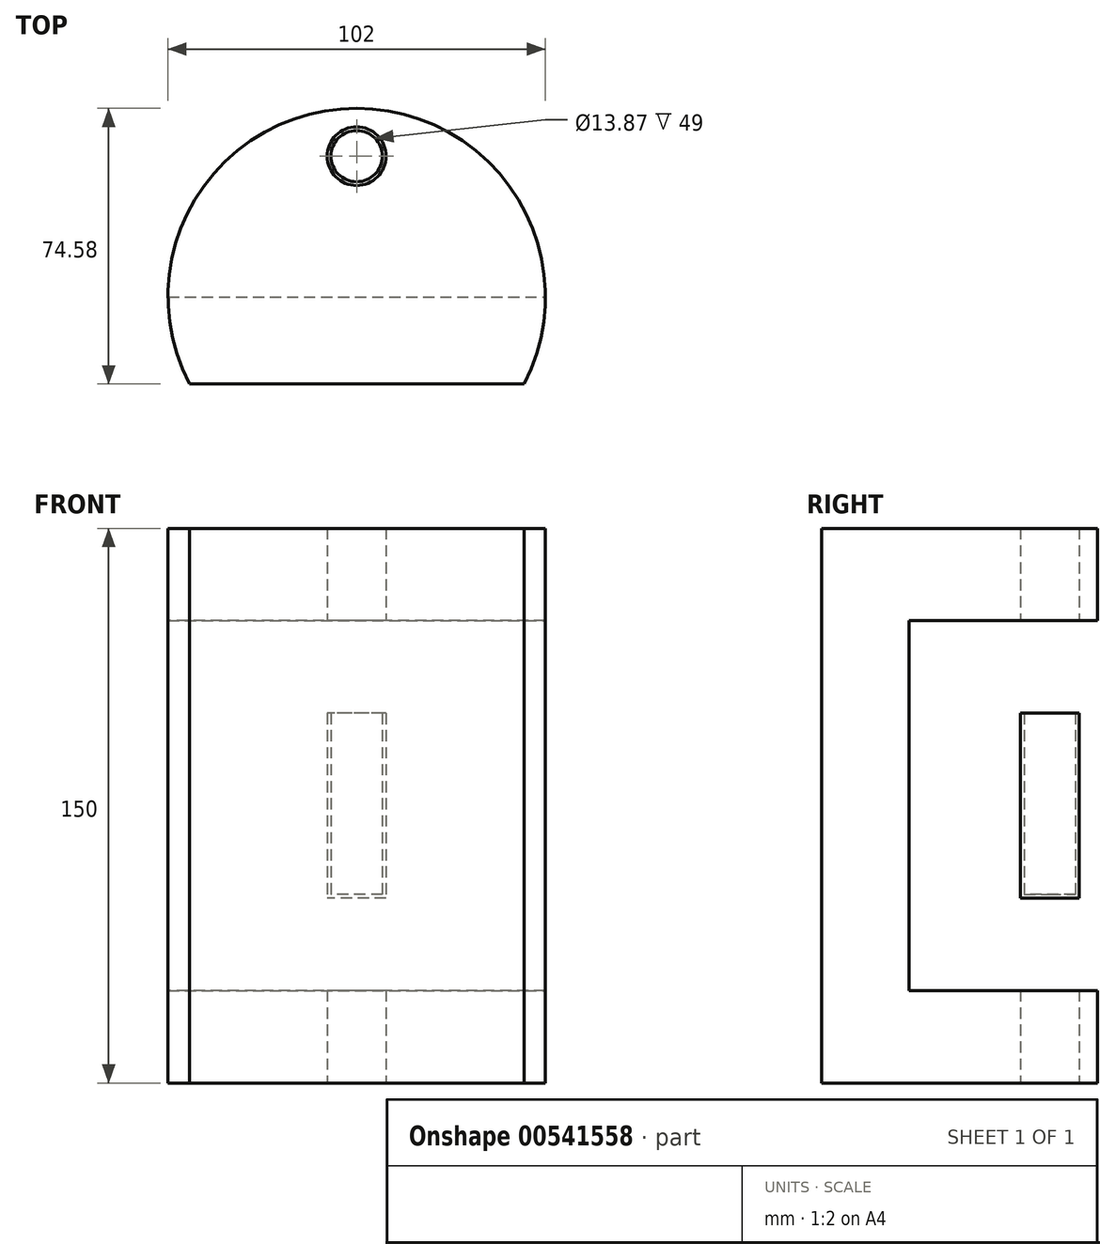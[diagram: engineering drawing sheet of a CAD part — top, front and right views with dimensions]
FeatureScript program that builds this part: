
annotation { "Feature Type Name" : "Feature", "Feature Type Description" : "" }
export const myFeature = defineFeature(function(context is Context, id is Id, definition is map)
    precondition{}
    {
        {
            var Q0;
            Q0=qCreatedBy(makeId("Top.planeOp"),FACE);
            var sketch = newSketch(context, id + "F0", { "sketchPlane" : qUnion([Q0])});
            skArc(sketch, "E0", {"start": v(45.22, -23.58) * mm, "mid": v(0, 51) * mm, "end": v(-45.22, -23.58) * mm});
            skLineSegment(sketch, "E1", {"start": v(0, -23.58) * mm, "end": v(45.22, -23.58) * mm});
            skLineSegment(sketch, "E2", {"start": v(0, -23.58) * mm, "end": v(-45.22, -23.58) * mm});
            skLineSegment(sketch, "E3", {"start": v(-51, 0) * mm, "end": v(51, 0) * mm});
            skCircle(sketch, "E4", {"center": v(0, 38.05) * mm, "radius": 7.94 * mm});
            skSolve(sketch);
        }
        {
            var Q0;
            {var subQ0=sQuery(id+"F0.wireOp",EDGE,"E3");Q0=makeQuery(id+"F0.imprint","IMPRINT",FACE,{"disambiguationData":[TD([[makeQuery(id+"F0.imprint","IMPRINT",EDGE,{"derivedFrom":subQ0}),1.0]])]});}
            extrude(context, id + "F1", {"entities" : qUnion([Q0]), "depth" : 75 * mm, "offsetDistance" : 25 * mm, "hasSecondDirection" : true, "secondDirectionOppositeDirection" : true, "secondDirectionDepth" : 75 * mm});
        }
        {
            var Q0;
            {var subQ1=sQuery(id+"F0.wireOp",EDGE,"E1");Q0=makeQuery(id+"F0.imprint","IMPRINT",FACE,{"disambiguationData":[TD([[makeQuery(id+"F0.imprint","IMPRINT",EDGE,{"derivedFrom":subQ1}),1.0]])]});}
            extrude(context, id + "F2", {"entities" : qUnion([Q0]), "operationType" : NewBodyOperationType.ADD, "depth" : 75 * mm, "offsetDistance" : 25 * mm, "hasSecondDirection" : true, "secondDirectionOppositeDirection" : true, "secondDirectionDepth" : 75 * mm});
        }
        {
            var Q0;
            {var subQ0=sQuery(id+"F0.wireOp",EDGE,"E3");Q0=makeQuery(id+"F0.imprint","IMPRINT",FACE,{"disambiguationData":[TD([[makeQuery(id+"F0.imprint","IMPRINT",EDGE,{"derivedFrom":subQ0}),1.0]])]});}
            extrude(context, id + "F3", {"entities" : qUnion([Q0]), "operationType" : NewBodyOperationType.REMOVE, "oppositeDirection" : true, "depth" : 50 * mm, "offsetDistance" : 25 * mm, "hasSecondDirection" : true, "secondDirectionOppositeDirection" : false, "secondDirectionDepth" : 50 * mm});
        }
        {
            var Q0;
            Q0=makeQuery(id+"F0.imprint","IMPRINT",FACE,{"disambiguationData":[TD([[makeQuery(id+"F0.imprint","IMPRINT",EDGE,{"derivedFrom":sQuery(id+"F0.wireOp",EDGE,"E4")}),1.0]])]});
            var Q1;
            Q1=sQuery(id+"F0.wireOp",EDGE,"E4");
            extrude(context, id + "F4", {"entities" : qUnion([Q0]), "surfaceEntities" : qUnion([Q1]), "depth" : 25 * mm, "offsetDistance" : 25 * mm, "hasSecondDirection" : true, "secondDirectionOppositeDirection" : true, "secondDirectionDepth" : 25 * mm});
        }
        {
            var Q0;
            Q0=makeQuery(id+"F4.opExtrude","CAP_FACE",FACE,{"disambiguationData":[OSD([sQuery(id+"F0.wireOp",EDGE,"E4")])],"isStart":false});
            shell(context, id + "F5", {"entities" : qUnion([Q0]), "thickness" : 1 * mm});
        }
    });
